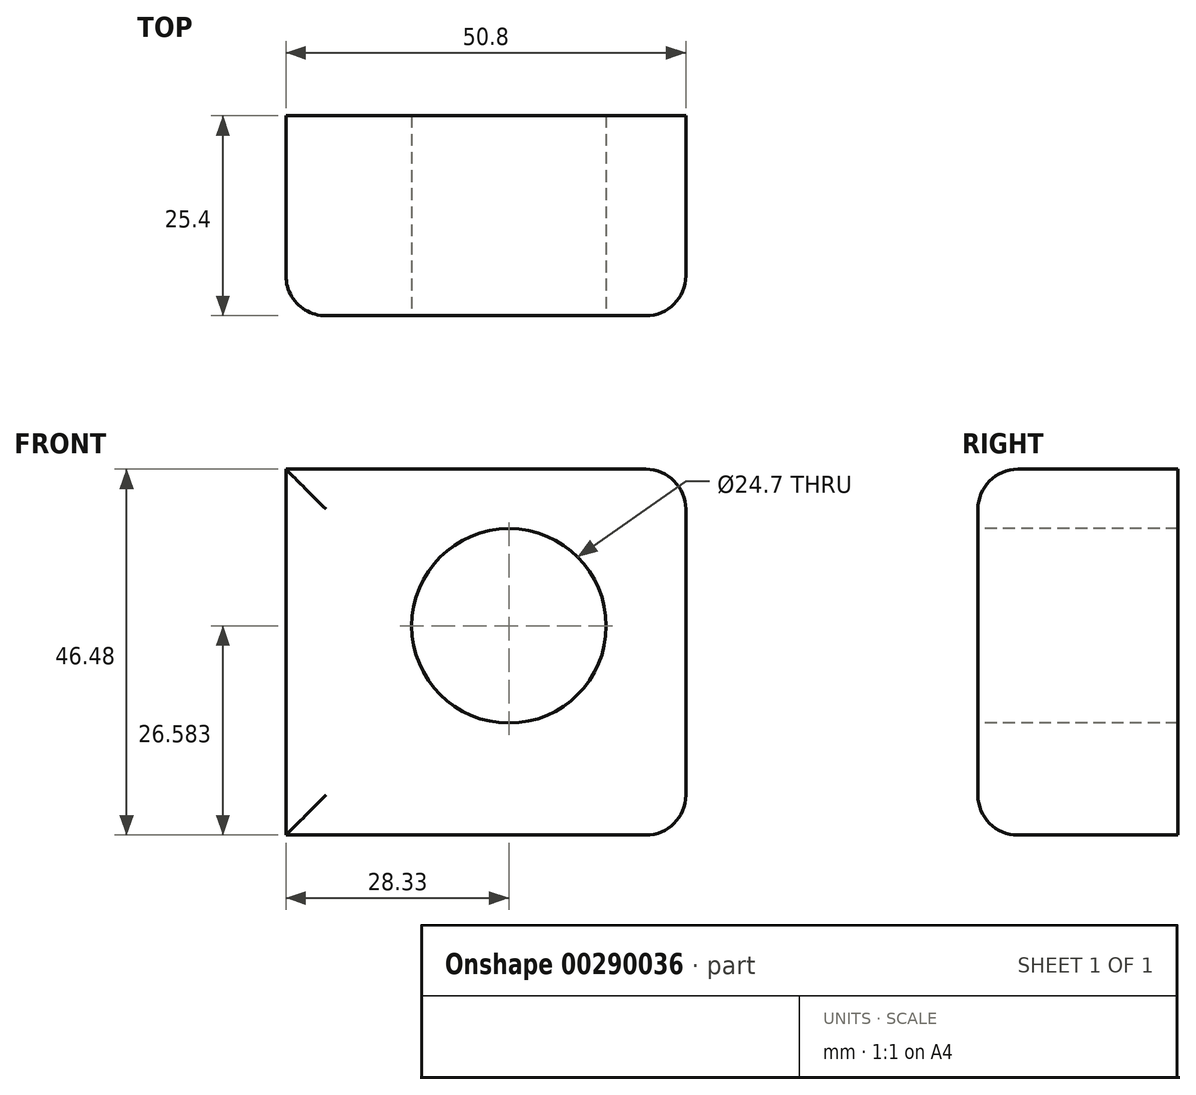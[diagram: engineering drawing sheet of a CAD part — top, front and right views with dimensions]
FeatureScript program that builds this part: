
annotation { "Feature Type Name" : "Feature", "Feature Type Description" : "" }
export const myFeature = defineFeature(function(context is Context, id is Id, definition is map)
    precondition{}
    {
        {
            var Q0;
            Q0=qCreatedBy(makeId("Top.planeOp"),FACE);
            var sketch = newSketch(context, id + "F0", { "sketchPlane" : qUnion([Q0])});
            skLineSegment(sketch, "E0.bottom", {"start": v(0, 0) * mm, "end": v(50.8, 0) * mm});
            skLineSegment(sketch, "E0.top", {"start": v(0, 25.4) * mm, "end": v(50.8, 25.4) * mm});
            skLineSegment(sketch, "E0.left", {"start": v(0, 0) * mm, "end": v(0, 25.4) * mm});
            skLineSegment(sketch, "E0.right", {"start": v(50.8, 0) * mm, "end": v(50.8, 25.4) * mm});
            skLineSegment(sketch, "E1", {"start": v(0, 0) * mm, "end": v(-36.42, 52.02) * mm});
            skCircle(sketch, "E2", {"center": v(-4.25, -2.79) * mm, "radius": 2.54 * mm});
            skSolve(sketch);
        }
        {
            var Q0;
            Q0=makeQuery(id+"F0.imprint","IMPRINT",FACE,{"disambiguationData":[TD([[makeQuery(id+"F0.imprint","IMPRINT",EDGE,{"derivedFrom":sQuery(id+"F0.wireOp",EDGE,"E0.bottom")}),1.0]])]});
            extrude(context, id + "F1", {"entities" : qUnion([Q0]), "depth" : 46.48 * mm});
        }
        {
            var Q0;
            Q0=makeQuery(id+"F1.opExtrude","SWEPT_FACE",FACE,{"disambiguationData":[OSD([sQuery(id+"F0.wireOp",EDGE,"E0.bottom")])]});
            var sketch = newSketch(context, id + "F2", { "sketchPlane" : qUnion([Q0])});
            skCircle(sketch, "E3", {"center": v(28.33, 26.58) * mm, "radius": 12.35 * mm});
            skSolve(sketch);
        }
        {
            var Q0;
            Q0=makeQuery(id+"F2.imprint","IMPRINT",FACE,{"disambiguationData":[TD([[makeQuery(id+"F2.imprint","IMPRINT",EDGE,{"derivedFrom":sQuery(id+"F2.wireOp",EDGE,"E3")}),1.0]])]});
            extrude(context, id + "F3", {"entities" : qUnion([Q0]), "operationType" : NewBodyOperationType.REMOVE, "oppositeDirection" : true, "depth" : 25.4 * mm});
        }
        {
            var Q0;
            Q0=makeQuery(id+"F1.opExtrude","SWEPT_EDGE",EDGE,{"disambiguationData":[OSD([sQuery(id+"F0.wireOp",EDGE,"E0.bottom"),sQuery(id+"F0.wireOp",EDGE,"E0.right")])]});
            fillet(context, id + "F4", {"entities" : qUnion([Q0]), "radius" : 5.08 * mm, "tangentPropagation" : true, "allowEdgeOverflow" : false});
        }
        {
            var Q0;
            Q0=makeQuery(id+"F1.opExtrude","CAP_EDGE",EDGE,{"disambiguationData":[OSD([sQuery(id+"F0.wireOp",EDGE,"E0.bottom")])],"isStart":true});
            var Q1;
            Q1=makeQuery(id+"F1.opExtrude","SWEPT_EDGE",EDGE,{"disambiguationData":[OSD([sQuery(id+"F0.wireOp",EDGE,"E0.bottom"),sQuery(id+"F0.wireOp",EDGE,"E0.left")])]});
            var Q2;
            Q2=makeQuery(id+"F1.opExtrude","CAP_EDGE",EDGE,{"disambiguationData":[OSD([sQuery(id+"F0.wireOp",EDGE,"E0.bottom")])],"isStart":false});
            fillet(context, id + "F5", {"entities" : qUnion([Q0, Q1, Q2]), "radius" : 5.08 * mm, "tangentPropagation" : true, "allowEdgeOverflow" : false});
        }
    });
